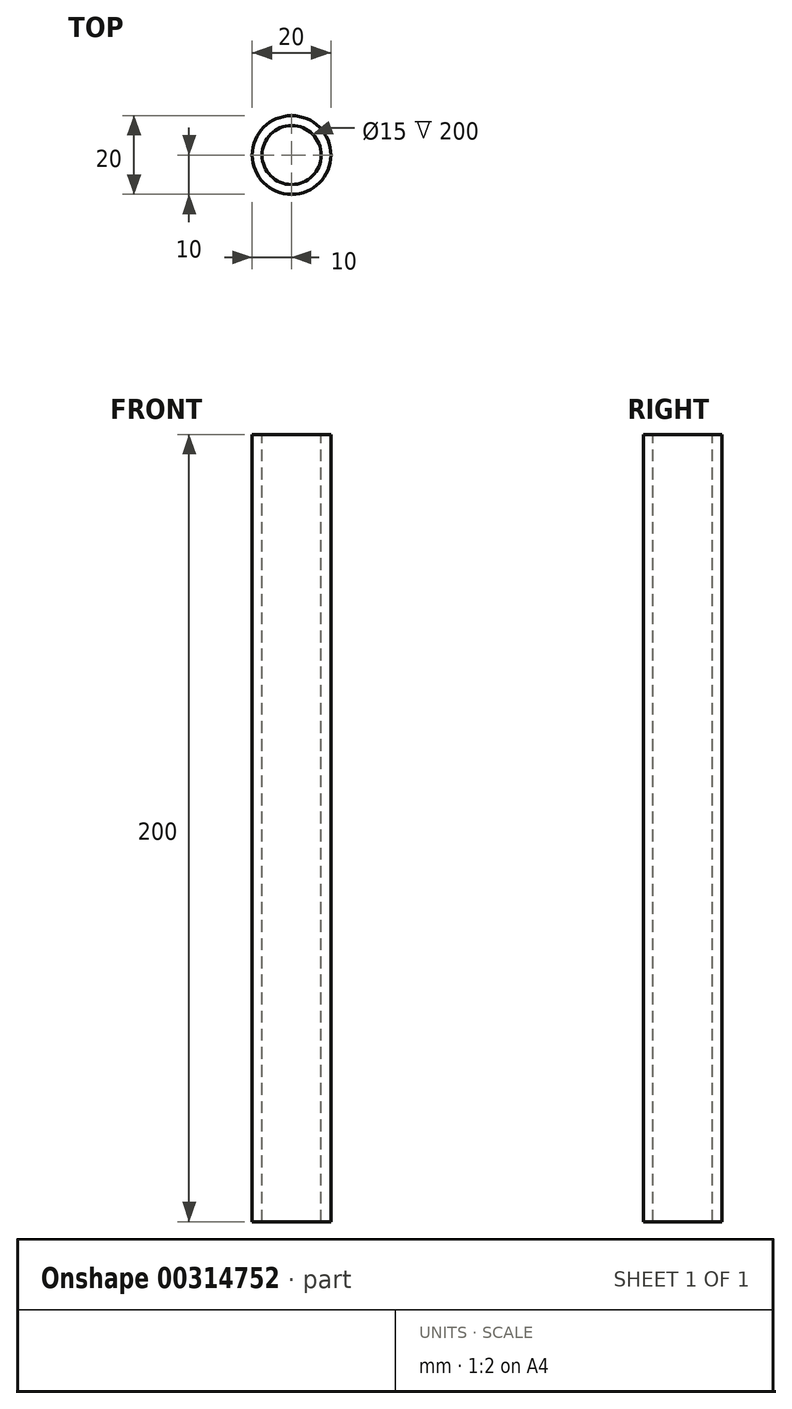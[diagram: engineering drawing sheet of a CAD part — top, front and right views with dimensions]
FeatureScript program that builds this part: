
annotation { "Feature Type Name" : "Feature", "Feature Type Description" : "" }
export const myFeature = defineFeature(function(context is Context, id is Id, definition is map)
    precondition{}
    {
        {
            var Q0;
            Q0=qCreatedBy(makeId("Top.planeOp"),FACE);
            var sketch = newSketch(context, id + "F0", { "sketchPlane" : qUnion([Q0])});
            skCircle(sketch, "E0", {"center": v(0, 0) * mm, "radius": 10 * mm});
            skSolve(sketch);
        }
        {
            var Q0;
            Q0 = qSketchRegion(id + "F0", true);
            extrude(context, id + "F1", {"entities" : qUnion([Q0]), "depth" : 200 * mm, "offsetDistance" : 25 * mm});
        }
        {
            var Q0;
            Q0=makeQuery(id+"F1.opExtrude","CAP_FACE",FACE,{"disambiguationData":[OSD([sQuery(id+"F0.wireOp",EDGE,"E0")])],"isStart":false});
            var sketch = newSketch(context, id + "F2", { "sketchPlane" : qUnion([Q0])});
            skCircle(sketch, "E1", {"center": v(0, 0) * mm, "radius": 1.5 * mm});
            skSolve(sketch);
        }
        {
            var Q0;
            Q0=makeQuery(id+"F1.opExtrude","CAP_FACE",FACE,{"disambiguationData":[OSD([sQuery(id+"F0.wireOp",EDGE,"E0")])],"isStart":true});
            var sketch = newSketch(context, id + "F3", { "sketchPlane" : qUnion([Q0])});
            skCircle(sketch, "E2", {"center": v(0, 0) * mm, "radius": 1.5 * mm});
            skSolve(sketch);
        }
        {
            var Q0;
            Q0=sQuery(id+"F3.wireOp",VERTEX,"E2.center");
            var Q1;
            Q1=makeQuery(id+"F1.opExtrude","SWEPT_BODY",BODY,{"disambiguationData":[OSD([sQuery(id+"F0.wireOp",EDGE,"E0")])]});
            hole(context, id + "F4", {"style" : HoleStyle.SIMPLE, "endStyle" : HoleEndStyle.BLIND, "holeDiameter" : 3 * mm, "holeDepth" : 100 * mm, "tappedDepth" : 12 * mm, "tapClearance" : 3, "locations" : qUnion([Q0]), "scope" : qUnion([Q1])});
        }
        {
            var Q0;
            Q0=makeQuery(id+"F2.imprint","IMPRINT",FACE,{"disambiguationData":[TD([[makeQuery(id+"F2.imprint","IMPRINT",EDGE,{"derivedFrom":sQuery(id+"F2.wireOp",EDGE,"E1")}),-1.0]])]});
            var sketch = newSketch(context, id + "F5", { "sketchPlane" : qUnion([Q0])});
            skCircle(sketch, "E3", {"center": v(0, 0) * mm, "radius": 8 * mm});
            skSolve(sketch);
        }
        {
            var Q0;
            Q0=sQuery(id+"F5.wireOp",VERTEX,"E3.center");
            var Q1;
            Q1=makeQuery(id+"F1.opExtrude","SWEPT_BODY",BODY,{"disambiguationData":[OSD([sQuery(id+"F0.wireOp",EDGE,"E0")])]});
            hole(context, id + "F6", {"style" : HoleStyle.SIMPLE, "endStyle" : HoleEndStyle.BLIND, "holeDiameter" : 15 * mm, "holeDepth" : 200 * mm, "tappedDepth" : 12 * mm, "tapClearance" : 3, "locations" : qUnion([Q0]), "scope" : qUnion([Q1])});
        }
    });
